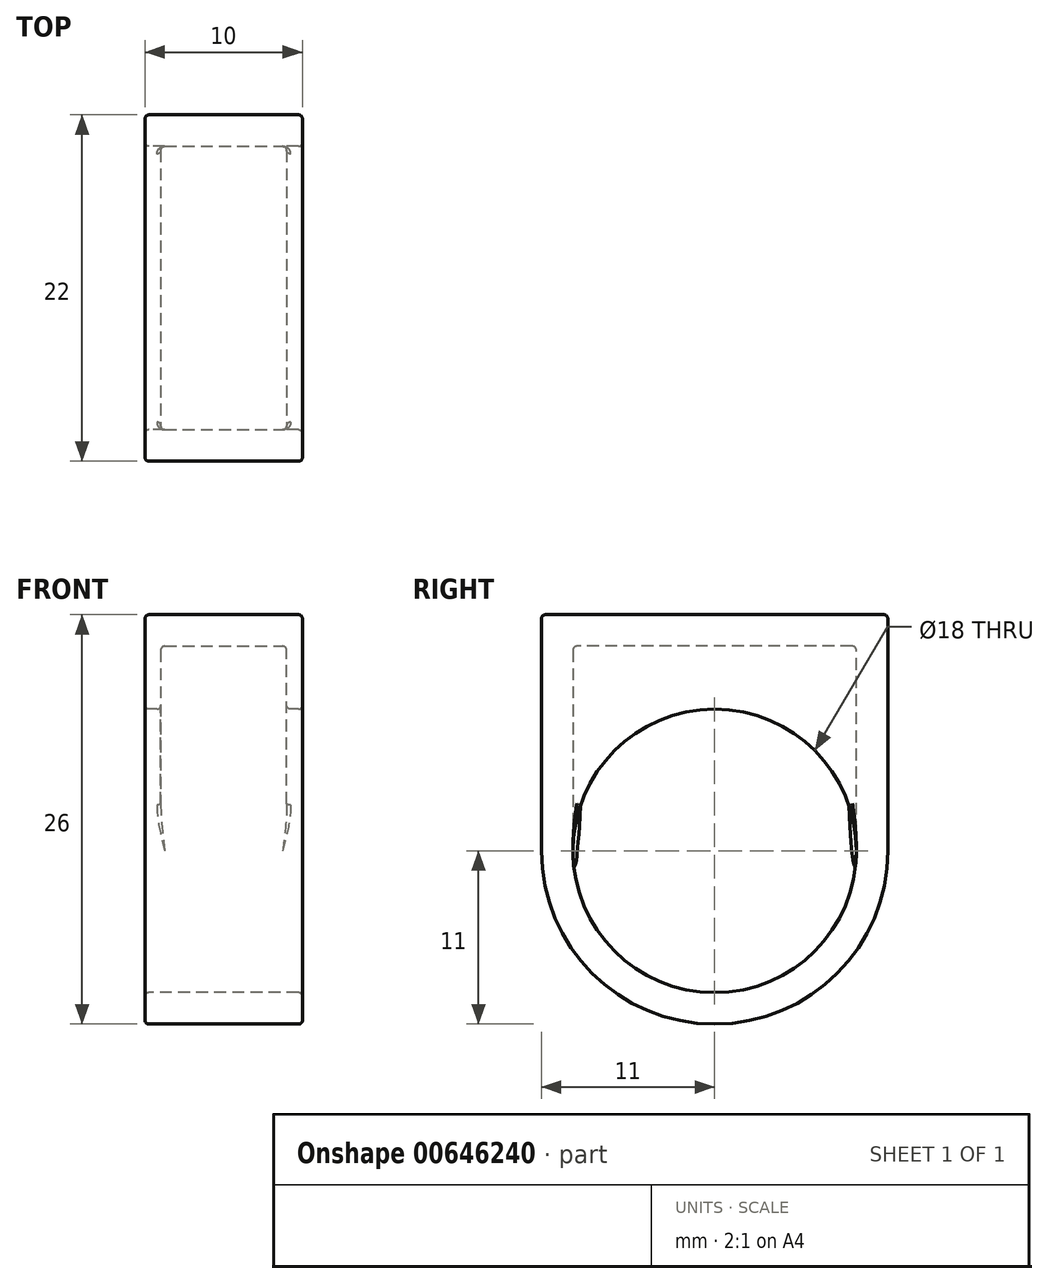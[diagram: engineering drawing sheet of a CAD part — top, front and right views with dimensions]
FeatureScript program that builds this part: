
annotation { "Feature Type Name" : "Feature", "Feature Type Description" : "" }
export const myFeature = defineFeature(function(context is Context, id is Id, definition is map)
    precondition{}
    {
        {
            var Q0;
            Q0=qCreatedBy(makeId("Right.planeOp"),FACE);
            var sketch = newSketch(context, id + "F0", { "sketchPlane" : qUnion([Q0])});
            skCircle(sketch, "E0", {"center": v(0, 0) * mm, "radius": 9 * mm});
            skArc(sketch, "E1", {"start": v(-11, 0) * mm, "mid": v(0, -11) * mm, "end": v(11, 0) * mm});
            skLineSegment(sketch, "E2", {"start": v(-11, 0) * mm, "end": v(-11, 15) * mm});
            skLineSegment(sketch, "E3", {"start": v(-11, 15) * mm, "end": v(-11, 15) * mm});
            skLineSegment(sketch, "E4", {"start": v(11, 0) * mm, "end": v(11, 15) * mm});
            skLineSegment(sketch, "E5", {"start": v(-11, 15) * mm, "end": v(11, 15) * mm});
            skSolve(sketch);
        }
        {
            var Q0;
            Q0 = qSketchRegion(id + "F0", true);
            extrude(context, id + "F1", {"entities" : qUnion([Q0]), "endBound" : BoundingType.SYMMETRIC, "depth" : 10 * mm, "offsetDistance" : 25 * mm});
        }
        {
            var Q0;
            Q0=qCreatedBy(makeId("Right.planeOp"),FACE);
            var sketch = newSketch(context, id + "F2", { "sketchPlane" : qUnion([Q0])});
            skLineSegment(sketch, "E6.0", {"start": v(9, 13) * mm, "end": v(-9, 13) * mm});
            skLineSegment(sketch, "E6.1", {"start": v(9, 0) * mm, "end": v(9, 13) * mm});
            skArc(sketch, "E6.2", {"start": v(-9, 0) * mm, "mid": v(0, -9) * mm, "end": v(9, 0) * mm});
            skLineSegment(sketch, "E6.3", {"start": v(-9, 13) * mm, "end": v(-9, 0) * mm});
            skSolve(sketch);
        }
        {
            var Q0;
            Q0 = qSketchRegion(id + "F2", true);
            extrude(context, id + "F3", {"entities" : qUnion([Q0]), "operationType" : NewBodyOperationType.REMOVE, "endBound" : BoundingType.SYMMETRIC, "oppositeDirection" : true, "depth" : 8 * mm, "offsetDistance" : 25 * mm});
        }
        {
            var Q0;
            Q0=makeQuery(id+"F1.opExtrude","CAP_EDGE",EDGE,{"disambiguationData":[OSD([sQuery(id+"F0.wireOp",EDGE,"E4")])],"isStart":false});
            var Q1;
            Q1=makeQuery(id+"F1.opExtrude","CAP_EDGE",EDGE,{"disambiguationData":[OSD([sQuery(id+"F0.wireOp",EDGE,"E4")])],"isStart":true});
            var Q2;
            Q2=makeQuery(id+"F1.opExtrude","CAP_EDGE",EDGE,{"disambiguationData":[OSD([sQuery(id+"F0.wireOp",EDGE,"E2")])],"isStart":false});
            var Q3;
            Q3=makeQuery(id+"F1.opExtrude","CAP_EDGE",EDGE,{"disambiguationData":[OSD([sQuery(id+"F0.wireOp",EDGE,"E5")])],"isStart":false});
            var Q4;
            Q4=makeQuery(id+"F1.opExtrude","CAP_EDGE",EDGE,{"disambiguationData":[OSD([sQuery(id+"F0.wireOp",EDGE,"E5")])],"isStart":true});
            var Q5;
            Q5=makeQuery(id+"F1.opExtrude","SWEPT_FACE",FACE,{"disambiguationData":[OSD([sQuery(id+"F0.wireOp",EDGE,"E5")])]});
            var Q6;
            Q6=makeQuery(id+"F1.opExtrude","CAP_EDGE",EDGE,{"disambiguationData":[OSD([sQuery(id+"F0.wireOp",EDGE,"E1")])],"isStart":false});
            var Q7;
            Q7=makeQuery(id+"F1.opExtrude","CAP_EDGE",EDGE,{"disambiguationData":[OSD([sQuery(id+"F0.wireOp",EDGE,"E1")])],"isStart":true});
            var Q8;
            Q8=makeQuery(id+"F1.opExtrude","CAP_EDGE",EDGE,{"disambiguationData":[OSD([sQuery(id+"F0.wireOp",EDGE,"E0")])],"isStart":false});
            var Q9;
            Q9=makeQuery(id+"F1.opExtrude","CAP_EDGE",EDGE,{"disambiguationData":[OSD([sQuery(id+"F0.wireOp",EDGE,"E0")])],"isStart":true});
            var Q10;
            Q10=makeQuery(id+"F1.opExtrude","SWEPT_EDGE",EDGE,{"disambiguationData":[OSD([sQuery(id+"F0.wireOp",EDGE,"E4"),sQuery(id+"F0.wireOp",EDGE,"E5")])]});
            var Q11;
            Q11=makeQuery(id+"F1.opExtrude","SWEPT_EDGE",EDGE,{"disambiguationData":[OSD([sQuery(id+"F0.wireOp",EDGE,"E2"),sQuery(id+"F0.wireOp",EDGE,"E5")])]});
            var Q12;
            Q12=makeQuery(id+"F3.boolean.opBoolean","COPY",EDGE,{"derivedFrom":makeQuery(id+"F3.opExtrude","SWEPT_EDGE",EDGE,{"disambiguationData":[OSD([sQuery(id+"F2.wireOp",EDGE,"E6.0"),sQuery(id+"F2.wireOp",EDGE,"E6.1")])]})});
            var Q13;
            Q13=makeQuery(id+"F3.boolean.opBoolean","COPY",EDGE,{"derivedFrom":makeQuery(id+"F3.opExtrude","SWEPT_EDGE",EDGE,{"disambiguationData":[OSD([sQuery(id+"F2.wireOp",EDGE,"E6.0"),sQuery(id+"F2.wireOp",EDGE,"E6.3")])]})});
            var Q14;
            Q14=makeQuery(id+"F3.boolean.opBoolean","COPY",EDGE,{"derivedFrom":makeQuery(id+"F3.opExtrude","CAP_EDGE",EDGE,{"disambiguationData":[OSD([sQuery(id+"F2.wireOp",EDGE,"E6.0")])],"isStart":true})});
            var Q15;
            Q15=makeQuery(id+"F3.boolean.opBoolean","INTERSECT",EDGE,{"derivedFrom":[makeQuery(id+"F1.opExtrude","SWEPT_FACE",FACE,{"disambiguationData":[OSD([sQuery(id+"F0.wireOp",EDGE,"E0")])]}),makeQuery(id+"F3.opExtrude","CAP_FACE",FACE,{"disambiguationData":[OSD([sQuery(id+"F2.wireOp",EDGE,"E6.0"),sQuery(id+"F2.wireOp",EDGE,"E6.1"),sQuery(id+"F2.wireOp",EDGE,"E6.2"),sQuery(id+"F2.wireOp",EDGE,"E6.3")])],"isStart":true})]});
            var Q16;
            Q16=makeQuery(id+"F1.opExtrude","CAP_EDGE",EDGE,{"disambiguationData":[OSD([sQuery(id+"F0.wireOp",EDGE,"E2")])],"isStart":true});
            var Q17;
            Q17=makeQuery(id+"F3.boolean.opBoolean","COPY",EDGE,{"derivedFrom":makeQuery(id+"F3.opExtrude","CAP_EDGE",EDGE,{"disambiguationData":[OSD([sQuery(id+"F2.wireOp",EDGE,"E6.0")])],"isStart":false})});
            var Q18;
            Q18=makeQuery(id+"F3.boolean.opBoolean","COPY",EDGE,{"derivedFrom":makeQuery(id+"F3.opExtrude","CAP_EDGE",EDGE,{"disambiguationData":[OSD([sQuery(id+"F2.wireOp",EDGE,"E6.1")])],"isStart":true})});
            var Q19;
            Q19=makeQuery(id+"F3.boolean.opBoolean","COPY",EDGE,{"derivedFrom":makeQuery(id+"F3.opExtrude","CAP_EDGE",EDGE,{"disambiguationData":[OSD([sQuery(id+"F2.wireOp",EDGE,"E6.1")])],"isStart":false})});
            var Q20;
            Q20=makeQuery(id+"F3.boolean.opBoolean","COPY",EDGE,{"derivedFrom":makeQuery(id+"F3.opExtrude","CAP_EDGE",EDGE,{"disambiguationData":[OSD([sQuery(id+"F2.wireOp",EDGE,"E6.3")])],"isStart":true})});
            var Q21;
            Q21=makeQuery(id+"F3.boolean.opBoolean","COPY",EDGE,{"derivedFrom":makeQuery(id+"F3.opExtrude","CAP_EDGE",EDGE,{"disambiguationData":[OSD([sQuery(id+"F2.wireOp",EDGE,"E6.3")])],"isStart":false})});
            var Q22;
            Q22=makeQuery(id+"F3.boolean.opBoolean","INTERSECT",EDGE,{"derivedFrom":[makeQuery(id+"F1.opExtrude","SWEPT_FACE",FACE,{"disambiguationData":[OSD([sQuery(id+"F0.wireOp",EDGE,"E0")])]}),makeQuery(id+"F3.opExtrude","CAP_FACE",FACE,{"disambiguationData":[OSD([sQuery(id+"F2.wireOp",EDGE,"E6.0"),sQuery(id+"F2.wireOp",EDGE,"E6.1"),sQuery(id+"F2.wireOp",EDGE,"E6.2"),sQuery(id+"F2.wireOp",EDGE,"E6.3")])],"isStart":false})]});
            var Q23;
            Q23=makeQuery(id+"F1.opExtrude","SWEPT_EDGE",EDGE,{"disambiguationData":[OSD([sQuery(id+"F0.wireOp",EDGE,"E1"),sQuery(id+"F0.wireOp",EDGE,"E4")])]});
            var Q24;
            Q24=makeQuery(id+"F3.boolean.opBoolean","COPY",EDGE,{"derivedFrom":makeQuery(id+"F3.opExtrude","SWEPT_EDGE",EDGE,{"disambiguationData":[OSD([sQuery(id+"F2.wireOp",EDGE,"E6.2"),sQuery(id+"F2.wireOp",EDGE,"E6.3")])]})});
            var Q25;
            Q25=makeQuery(id+"F1.opExtrude","SWEPT_EDGE",EDGE,{"disambiguationData":[OSD([sQuery(id+"F0.wireOp",EDGE,"E1"),sQuery(id+"F0.wireOp",EDGE,"E2")])]});
            var Q26;
            Q26=makeQuery(id+"F3.boolean.opBoolean","COPY",EDGE,{"derivedFrom":makeQuery(id+"F3.opExtrude","SWEPT_EDGE",EDGE,{"disambiguationData":[OSD([sQuery(id+"F2.wireOp",EDGE,"E6.1"),sQuery(id+"F2.wireOp",EDGE,"E6.2")])]})});
            fillet(context, id + "F4", {"entities" : qUnion([Q0, Q1, Q2, Q3, Q4, Q5, Q6, Q7, Q8, Q9, Q10, Q11, Q12, Q13, Q14, Q15, Q16, Q17, Q18, Q19, Q20, Q21, Q22, Q23, Q24, Q25, Q26]), "radius" : 0.25 * mm, "tangentPropagation" : true, "allowEdgeOverflow" : false});
        }
    });
